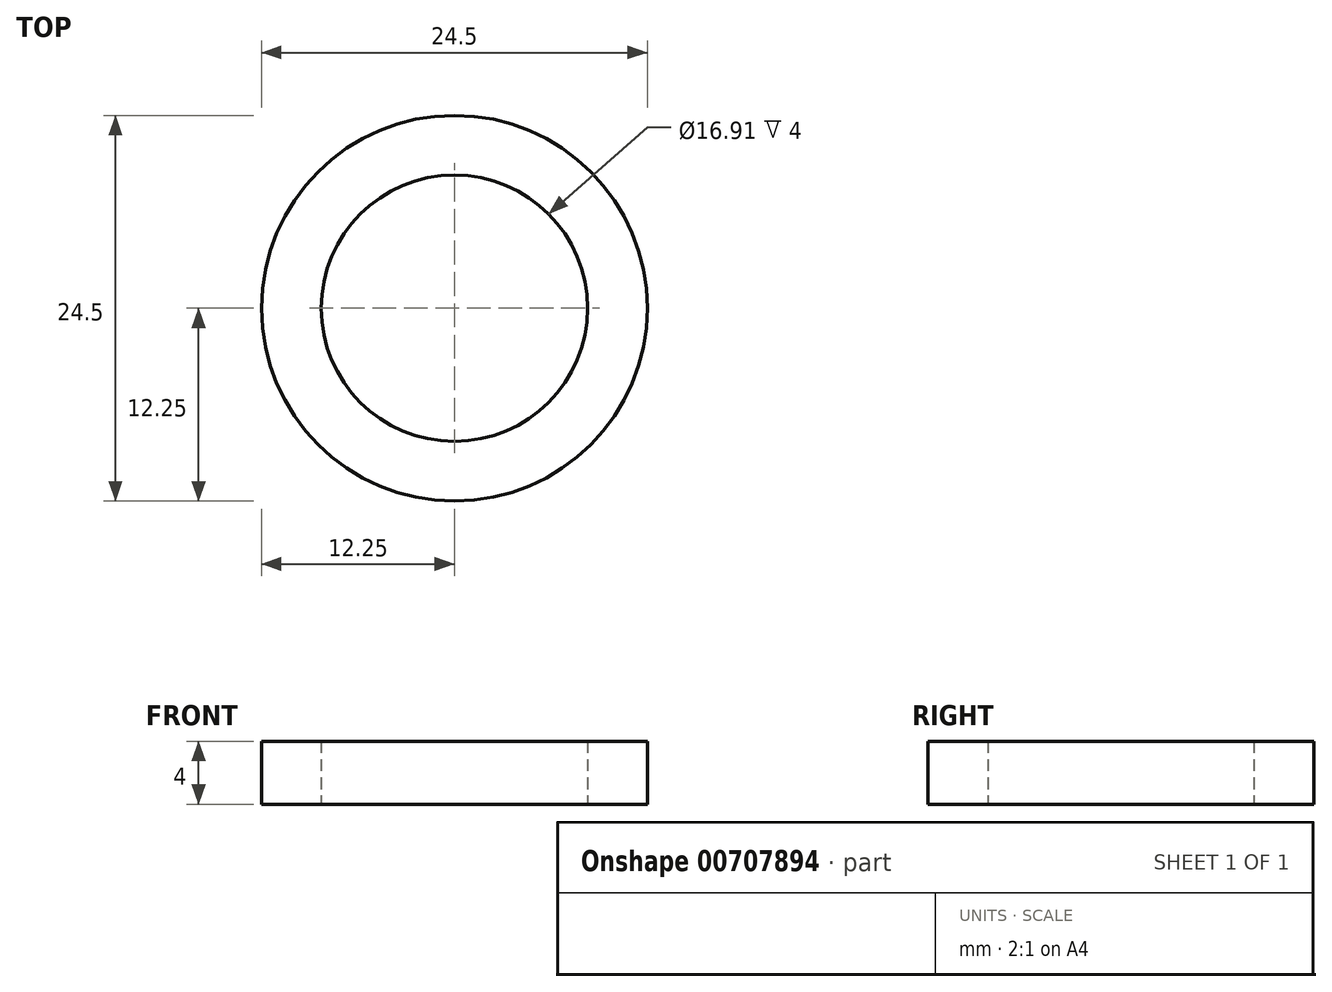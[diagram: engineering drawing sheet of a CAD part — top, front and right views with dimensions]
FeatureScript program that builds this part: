
annotation { "Feature Type Name" : "Feature", "Feature Type Description" : "" }
export const myFeature = defineFeature(function(context is Context, id is Id, definition is map)
    precondition{}
    {
        {
            var Q0;
            Q0=qCreatedBy(makeId("Top.planeOp"),FACE);
            var sketch = newSketch(context, id + "F0", { "sketchPlane" : qUnion([Q0])});
            skCircle(sketch, "E0", {"center": v(0, 0) * mm, "radius": 12.25 * mm});
            skCircle(sketch, "E1", {"center": v(0, 0) * mm, "radius": 8.46 * mm});
            skSolve(sketch);
        }
        {
            var Q0;
            Q0=makeQuery(id+"F0.imprint","IMPRINT",FACE,{"disambiguationData":[TD([[makeQuery(id+"F0.imprint","IMPRINT",EDGE,{"derivedFrom":sQuery(id+"F0.wireOp",EDGE,"E0")}),1.0]])]});
            extrude(context, id + "F1", {"entities" : qUnion([Q0]), "depth" : 4 * mm, "offsetDistance" : 25 * mm});
        }
    });
